# Revit family: Wall-Panel_Operable-Partition_Moderco_GymDoor-Series-DoorSingle
name_source: partatom
category: Curtain Panels
units: mm (PartAtom-declared; Revit-internal decimal feet)

## family parameters
Always vertical = Yes
Classification Number = 23.25.40.17
Cut with Voids When Loaded = No
Shared = No

## types (2) — shared parameters
Assembly Code = C1010300
Construction Details = http://www.arcat.com
Keynote = 10 22 26
Manufacturer = Moderco, Inc
Manufacturer Fax = 450-641-4965 or 800-231-4965
Manufacturer Website = http://moderco.com
Max Height = 30' - 0"
Panel Thickness = 0' - 3"
Product Data = http://www.arcat.com
Revision = R1_2015-09
Sales Information = http://moderco.com
Specification = http://www.arcat.com
Type Comments = Glazing is not included with the Wall Panel.
URL = http://moderco.com
Use = Electric Pair
zero-valued in all types: Expected Lifespan (Years), Maintenance Schedule (Months), Warranty Duration (Years)

## per-type parameters (varying)
| type | Description | Model |
| 8011 Electric Paired Panel | Moderco GymDoor Series 8011 Paired Single Door Panel as Specified | 8011 |
| 8010 Electric Paired Panel | Moderco GymDoor Series 8010 Paired Single Door Panel as Specified | 8010 |

## geometry (parser evidence)
native form markers: Sweep x7
no freeform markers — native parametric forms only
